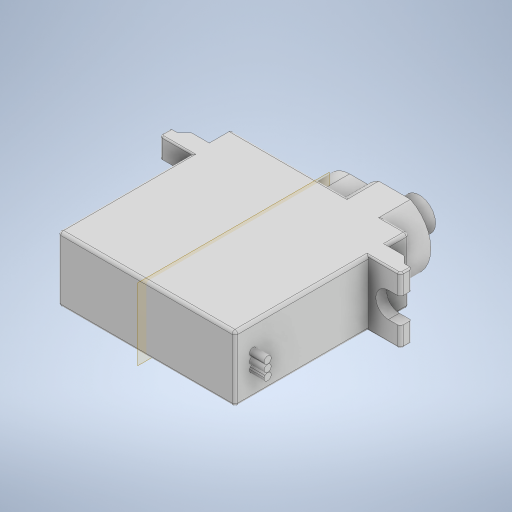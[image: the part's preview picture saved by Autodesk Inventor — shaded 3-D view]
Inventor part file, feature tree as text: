
AUTODESK INVENTOR PART (.ipt)
format: ipt  version: 2023 (Build 270158000, 158)  size: 451,584 bytes
history: native  units: mm
features: extrude x7, sketch x7, projected_geometry x5, fillet x3, other x2, mirror x1
ambient origin geometry x8: Origin, YZ Plane, XZ Plane, XY Plane, X Axis, Y Axis, Z Axis, Center Point
bodies: Body1 (feature_tree)
feature tree (25):
  other  "Bryła1"
  extrude  "Wyciągnięcie proste1"  Depth=24.4mm
  extrude  "Wyciągnięcie proste2"  Depth=24.0mm
  extrude  "Wyciągnięcie proste3"  Depth=9.0mm TaperAngle=0.0deg
  extrude  "Wyciągnięcie proste4"  Depth=18.4mm
  other  "Płaszczyzna konstrukcyjna1"
  mirror  "Odbij1"
  extrude  "Wyciągnięcie proste5"  Depth=1.5mm
  extrude  "Wyciągnięcie proste6"  Depth=2.46mm
  fillet  "Zaokrąglenie1"  Radius=1.5mm
  fillet  "Zaokrąglenie2"  Radius=1.5mm
  fillet  "Zaokrąglenie3"  Radius=4.4mm
  extrude  "Wyciągnięcie proste7"  Depth=1.0mm
  sketch  "Szkic1"
  sketch  "Szkic2"
  projected_geometry  "Pętla rzutowana1"
  sketch  "Szkic3"
  projected_geometry  "Pętla rzutowana2"
  sketch  "Szkic4"
  projected_geometry  "Pętla rzutowana3"
  sketch  "Szkic5"
  projected_geometry  "Pętla rzutowana4"
  sketch  "Szkic6"
  projected_geometry  "Pętla rzutowana5"
  sketch  "Szkic7"
